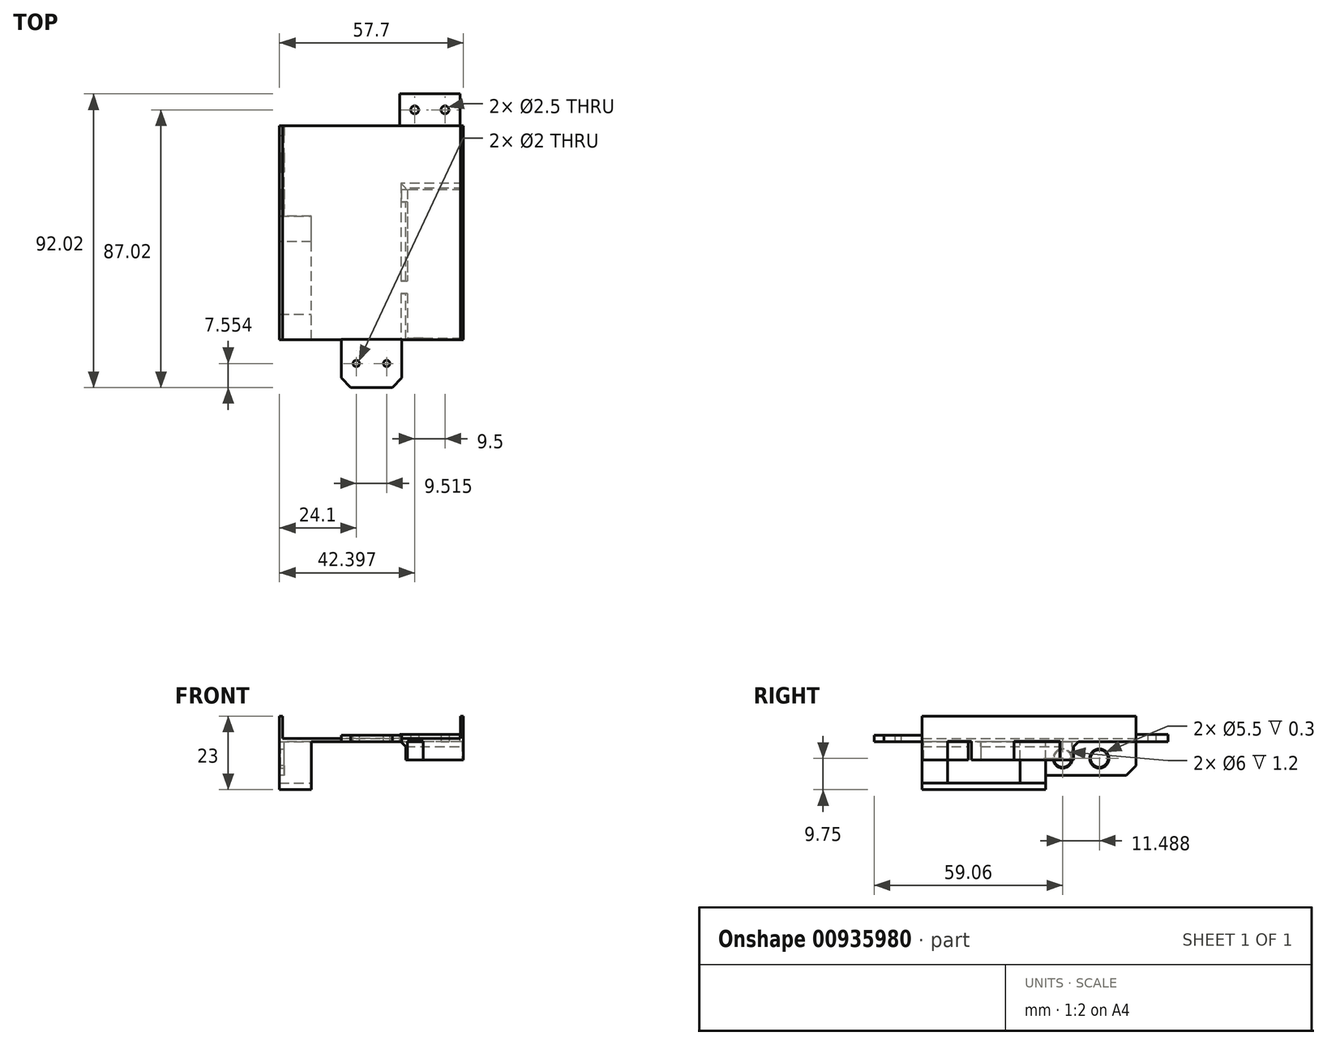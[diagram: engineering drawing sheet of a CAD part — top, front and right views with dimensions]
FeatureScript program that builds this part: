
annotation { "Feature Type Name" : "Feature", "Feature Type Description" : "" }
export const myFeature = defineFeature(function(context is Context, id is Id, definition is map)
    precondition{}
    {
        {
            var Q0;
            Q0=qCreatedBy(makeId("Top.planeOp"),FACE);
            var sketch = newSketch(context, id + "F0", { "sketchPlane" : qUnion([Q0])});
            skLineSegment(sketch, "E0.bottom", {"start": v(28.35, -33.5) * mm, "end": v(-28.35, -33.5) * mm});
            skLineSegment(sketch, "E0.top", {"start": v(28.35, 33.5) * mm, "end": v(-28.35, 33.5) * mm});
            skLineSegment(sketch, "E0.left", {"start": v(28.35, -33.5) * mm, "end": v(28.35, 33.5) * mm});
            skLineSegment(sketch, "E0.right", {"start": v(-28.35, -33.5) * mm, "end": v(-28.35, 33.5) * mm});
            skPoint(sketch, "E0.middle", {"position": v(0, 0) * mm});
            skLineSegment(sketch, "E1.bottom", {"start": v(27.85, -33.5) * mm, "end": v(-27.85, -33.5) * mm});
            skLineSegment(sketch, "E1.top", {"start": v(27.85, 33.5) * mm, "end": v(-27.85, 33.5) * mm});
            skLineSegment(sketch, "E1.left", {"start": v(27.85, -33.5) * mm, "end": v(27.85, 33.5) * mm});
            skLineSegment(sketch, "E1.right", {"start": v(-27.85, -33.5) * mm, "end": v(-27.85, 33.5) * mm});
            skSolve(sketch);
        }
        {
            var Q0;
            {var subQ0=sQuery(id+"F0.wireOp",EDGE,"E1.left");Q0=makeQuery(id+"F0.imprint","IMPRINT",FACE,{"disambiguationData":[TD([[makeQuery(id+"F0.imprint","IMPRINT",EDGE,{"derivedFrom":subQ0}),1.0]])]});}
            extrude(context, id + "F1", {"entities" : qUnion([Q0]), "depth" : 1 * mm, "offsetDistance" : 25 * mm});
        }
        {
            var Q0;
            Q0=makeQuery(id+"F1.opExtrude","CAP_FACE",FACE,{"disambiguationData":[OSD([sQuery(id+"F0.wireOp",EDGE,"E0.bottom"),sQuery(id+"F0.wireOp",EDGE,"E0.top"),sQuery(id+"F0.wireOp",EDGE,"E1.left"),sQuery(id+"F0.wireOp",EDGE,"E1.right")])],"isStart":false});
            var sketch = newSketch(context, id + "F2", { "sketchPlane" : qUnion([Q0])});
            skLineSegment(sketch, "E2.left", {"start": v(28.35, -33.5) * mm, "end": v(28.35, 33.5) * mm});
            skLineSegment(sketch, "E2.right", {"start": v(-28.35, -33.5) * mm, "end": v(-28.35, 33.5) * mm});
            skPoint(sketch, "E2.middle", {"position": v(0, 0) * mm});
            skLineSegment(sketch, "E3", {"start": v(-27.85, 33.5) * mm, "end": v(-28.35, 33.5) * mm});
            skLineSegment(sketch, "E4", {"start": v(27.85, 33.5) * mm, "end": v(28.35, 33.5) * mm});
            skLineSegment(sketch, "E5", {"start": v(-27.85, -33.5) * mm, "end": v(-28.35, -33.5) * mm});
            skLineSegment(sketch, "E6", {"start": v(27.85, -33.5) * mm, "end": v(28.35, -33.5) * mm});
            skPoint(sketch, "E7.orphan", {"position": v(28.35, -35) * mm});
            skPoint(sketch, "E8.orphan", {"position": v(-28.35, -35) * mm});
            skPoint(sketch, "E9.orphan", {"position": v(-28.35, 35) * mm});
            skPoint(sketch, "E10.orphan", {"position": v(28.35, 35) * mm});
            skSolve(sketch);
        }
        {
            var Q0;
            Q0=makeQuery(id+"F2.imprint","IMPRINT",FACE,{"disambiguationData":[TD([[makeQuery(id+"F2.imprint","IMPRINT",EDGE,{"derivedFrom":sQuery(id+"F2.wireOp",EDGE,"E2.right")}),-1.0]])]});
            extrude(context, id + "F3", {"entities" : qUnion([Q0]), "depth" : 7 * mm, "offsetDistance" : 25 * mm});
        }
        {
            var Q0;
            Q0=makeQuery(id+"F1.opExtrude","CAP_FACE",FACE,{"disambiguationData":[OSD([sQuery(id+"F0.wireOp",EDGE,"E0.bottom"),sQuery(id+"F0.wireOp",EDGE,"E0.top"),sQuery(id+"F0.wireOp",EDGE,"E1.left"),sQuery(id+"F0.wireOp",EDGE,"E1.right")])],"isStart":false});
            var sketch = newSketch(context, id + "F4", { "sketchPlane" : qUnion([Q0])});
            skLineSegment(sketch, "E11.bottom", {"start": v(27.85, 33.5) * mm, "end": v(28.85, 33.5) * mm});
            skLineSegment(sketch, "E11.top", {"start": v(27.85, -33.5) * mm, "end": v(28.85, -33.5) * mm});
            skLineSegment(sketch, "E11.left", {"start": v(27.85, 33.5) * mm, "end": v(27.85, -33.5) * mm});
            skLineSegment(sketch, "E11.right", {"start": v(28.85, 33.5) * mm, "end": v(28.85, -33.5) * mm});
            skSolve(sketch);
        }
        {
            var Q0;
            Q0 = qSketchRegion(id + "F4", true);
            extrude(context, id + "F5", {"entities" : qUnion([Q0]), "depth" : 7 * mm, "offsetDistance" : 25 * mm});
        }
        {
            var Q0;
            Q0=makeQuery(id+"F3.opExtrude","SWEPT_FACE",FACE,{"disambiguationData":[OSD([sQuery(id+"F2.wireOp",EDGE,"E2.right")])]});
            extrude(context, id + "F6", {"entities" : qUnion([Q0]), "operationType" : NewBodyOperationType.ADD, "depth" : .5 * mm, "offsetDistance" : 25 * mm});
        }
        {
            var Q0;
            {var subQ0=sQuery(id+"F2.wireOp",EDGE,"E2.right");Q0=makeQuery(id+"F6.boolean.opBoolean","MERGE",FACE,{"derivedFrom":[makeQuery(id+"F3.opExtrude","CAP_FACE",FACE,{"disambiguationData":[OSD([sQuery(id+"F0.wireOp",EDGE,"E1.right"),subQ0,sQuery(id+"F2.wireOp",EDGE,"E3"),sQuery(id+"F2.wireOp",EDGE,"E5")])],"isStart":true}),makeQuery(id+"F6.opExtrude","SWEPT_FACE",FACE,{"disambiguationData":[OSD([subQ0]),TDD([makeQuery(id+"F3.opExtrude","CAP_EDGE",EDGE,{"disambiguationData":[OSD([subQ0])],"isStart":true})])]})]});}
            extrude(context, id + "F7", {"entities" : qUnion([Q0]), "depth" : 1 * mm, "offsetDistance" : 25 * mm});
        }
        {
            var Q0;
            Q0=makeQuery(id+"F7.opExtrude","SWEPT_BODY",BODY,{"disambiguationData":[OSD([sQuery(id+"F0.wireOp",EDGE,"E1.right"),sQuery(id+"F2.wireOp",EDGE,"E2.right"),sQuery(id+"F2.wireOp",EDGE,"E3"),sQuery(id+"F2.wireOp",EDGE,"E5")])]});
            var Q1;
            Q1=makeQuery(id+"F1.opExtrude","SWEPT_BODY",BODY,{"disambiguationData":[OSD([sQuery(id+"F0.wireOp",EDGE,"E0.bottom"),sQuery(id+"F0.wireOp",EDGE,"E0.top"),sQuery(id+"F0.wireOp",EDGE,"E1.left"),sQuery(id+"F0.wireOp",EDGE,"E1.right")])]});
            var Q2;
            Q2=makeQuery(id+"F3.opExtrude","SWEPT_BODY",BODY,{"disambiguationData":[OSD([sQuery(id+"F0.wireOp",EDGE,"E1.right"),sQuery(id+"F2.wireOp",EDGE,"E2.right"),sQuery(id+"F2.wireOp",EDGE,"E3"),sQuery(id+"F2.wireOp",EDGE,"E5")])]});
            booleanBodies(context, id + "F8", {"operationType" : BooleanOperationType.UNION, "tools" : qUnion([Q0, Q1, Q2])});
        }
        {
            var Q0;
            Q0=makeQuery(id+"F5.opExtrude","CAP_FACE",FACE,{"disambiguationData":[OSD([sQuery(id+"F4.wireOp",EDGE,"E11.bottom"),sQuery(id+"F4.wireOp",EDGE,"E11.top"),sQuery(id+"F4.wireOp",EDGE,"E11.left"),sQuery(id+"F4.wireOp",EDGE,"E11.right")])],"isStart":true});
            extrude(context, id + "F9", {"entities" : qUnion([Q0]), "depth" : 1 * mm, "offsetDistance" : 25 * mm});
        }
        {
            var Q0;
            Q0=makeQuery(id+"F7.opExtrude","SWEPT_BODY",BODY,{"disambiguationData":[OSD([sQuery(id+"F0.wireOp",EDGE,"E1.right"),sQuery(id+"F2.wireOp",EDGE,"E2.right"),sQuery(id+"F2.wireOp",EDGE,"E3"),sQuery(id+"F2.wireOp",EDGE,"E5")])]});
            var Q1;
            Q1=makeQuery(id+"F9.opExtrude","SWEPT_BODY",BODY,{"disambiguationData":[OSD([sQuery(id+"F4.wireOp",EDGE,"E11.bottom"),sQuery(id+"F4.wireOp",EDGE,"E11.top"),sQuery(id+"F4.wireOp",EDGE,"E11.left"),sQuery(id+"F4.wireOp",EDGE,"E11.right")])]});
            var Q2;
            Q2=makeQuery(id+"F5.opExtrude","SWEPT_BODY",BODY,{"disambiguationData":[OSD([sQuery(id+"F4.wireOp",EDGE,"E11.bottom"),sQuery(id+"F4.wireOp",EDGE,"E11.top"),sQuery(id+"F4.wireOp",EDGE,"E11.left"),sQuery(id+"F4.wireOp",EDGE,"E11.right")])]});
            booleanBodies(context, id + "F10", {"operationType" : BooleanOperationType.UNION, "tools" : qUnion([Q0, Q1, Q2])});
        }
        {
            var Q0;
            {var subQ0=sQuery(id+"F0.wireOp",EDGE,"E1.right");Q0=makeQuery(id+"F10.opBoolean","MERGE",FACE,{"derivedFrom":[makeQuery(id+"F8.opBoolean","MERGE",FACE,{"derivedFrom":[makeQuery(id+"F1.opExtrude","CAP_FACE",FACE,{"disambiguationData":[OSD([sQuery(id+"F0.wireOp",EDGE,"E0.bottom"),sQuery(id+"F0.wireOp",EDGE,"E0.top"),sQuery(id+"F0.wireOp",EDGE,"E1.left"),subQ0])],"isStart":true}),makeQuery(id+"F7.opExtrude","CAP_FACE",FACE,{"disambiguationData":[OSD([subQ0,sQuery(id+"F2.wireOp",EDGE,"E2.right"),sQuery(id+"F2.wireOp",EDGE,"E3"),sQuery(id+"F2.wireOp",EDGE,"E5")])],"isStart":false})]}),makeQuery(id+"F9.opExtrude","CAP_FACE",FACE,{"disambiguationData":[OSD([sQuery(id+"F4.wireOp",EDGE,"E11.bottom"),sQuery(id+"F4.wireOp",EDGE,"E11.top"),sQuery(id+"F4.wireOp",EDGE,"E11.left"),sQuery(id+"F4.wireOp",EDGE,"E11.right")])],"isStart":false})]});}
            var sketch = newSketch(context, id + "F11", { "sketchPlane" : qUnion([Q0])});
            skLineSegment(sketch, "E12.bottom", {"start": v(-28.85, 33.5) * mm, "end": v(-18.85, 33.5) * mm});
            skLineSegment(sketch, "E12.top", {"start": v(-28.85, 25.5) * mm, "end": v(-18.85, 25.5) * mm});
            skLineSegment(sketch, "E12.left", {"start": v(-28.85, 33.5) * mm, "end": v(-28.85, 25.5) * mm});
            skLineSegment(sketch, "E12.right", {"start": v(-18.85, 33.5) * mm, "end": v(-18.85, 25.5) * mm});
            skSolve(sketch);
        }
        {
            var Q0;
            Q0 = qSketchRegion(id + "F11", true);
            extrude(context, id + "F12", {"entities" : qUnion([Q0]), "operationType" : NewBodyOperationType.ADD, "depth" : 13 * mm, "offsetDistance" : 25 * mm});
        }
        {
            var Q0;
            {var subQ0=sQuery(id+"F0.wireOp",EDGE,"E1.right");Q0=makeQuery(id+"F10.opBoolean","MERGE",FACE,{"derivedFrom":[makeQuery(id+"F8.opBoolean","MERGE",FACE,{"derivedFrom":[makeQuery(id+"F1.opExtrude","CAP_FACE",FACE,{"disambiguationData":[OSD([sQuery(id+"F0.wireOp",EDGE,"E0.bottom"),sQuery(id+"F0.wireOp",EDGE,"E0.top"),sQuery(id+"F0.wireOp",EDGE,"E1.left"),subQ0])],"isStart":true}),makeQuery(id+"F7.opExtrude","CAP_FACE",FACE,{"disambiguationData":[OSD([subQ0,sQuery(id+"F2.wireOp",EDGE,"E2.right"),sQuery(id+"F2.wireOp",EDGE,"E3"),sQuery(id+"F2.wireOp",EDGE,"E5")])],"isStart":false})]}),makeQuery(id+"F9.opExtrude","CAP_FACE",FACE,{"disambiguationData":[OSD([sQuery(id+"F4.wireOp",EDGE,"E11.bottom"),sQuery(id+"F4.wireOp",EDGE,"E11.top"),sQuery(id+"F4.wireOp",EDGE,"E11.left"),sQuery(id+"F4.wireOp",EDGE,"E11.right")])],"isStart":false})]});}
            var sketch = newSketch(context, id + "F13", { "sketchPlane" : qUnion([Q0])});
            skLineSegment(sketch, "E13", {"start": v(-18.85, 25.5) * mm, "end": v(-18.85, 2.82) * mm});
            skLineSegment(sketch, "E14.bottom", {"start": v(-18.85, 2.82) * mm, "end": v(-28.85, 2.82) * mm});
            skLineSegment(sketch, "E14.top", {"start": v(-18.85, -5.18) * mm, "end": v(-28.85, -5.18) * mm});
            skLineSegment(sketch, "E14.left", {"start": v(-18.85, 2.82) * mm, "end": v(-18.85, -5.18) * mm});
            skLineSegment(sketch, "E14.right", {"start": v(-28.85, 2.82) * mm, "end": v(-28.85, -5.18) * mm});
            skSolve(sketch);
        }
        {
            var Q0;
            Q0=makeQuery(id+"F13.imprint","IMPRINT",FACE,{"disambiguationData":[TD([[makeQuery(id+"F13.imprint","IMPRINT",EDGE,{"derivedFrom":sQuery(id+"F13.wireOp",EDGE,"E14.bottom")}),1.0]])]});
            extrude(context, id + "F14", {"entities" : qUnion([Q0]), "operationType" : NewBodyOperationType.ADD, "depth" : 13 * mm, "offsetDistance" : 25 * mm});
        }
        {
            var Q0;
            Q0=makeQuery(id+"F12.opExtrude","CAP_FACE",FACE,{"disambiguationData":[OSD([sQuery(id+"F11.wireOp",EDGE,"E12.bottom"),sQuery(id+"F11.wireOp",EDGE,"E12.top"),sQuery(id+"F11.wireOp",EDGE,"E12.left"),sQuery(id+"F11.wireOp",EDGE,"E12.right")])],"isStart":false});
            var sketch = newSketch(context, id + "F15", { "sketchPlane" : qUnion([Q0])});
            skLineSegment(sketch, "E15.bottom", {"start": v(-28.85, 33.5) * mm, "end": v(-18.83, 33.5) * mm});
            skLineSegment(sketch, "E15.top", {"start": v(-28.85, -5.2) * mm, "end": v(-18.83, -5.2) * mm});
            skLineSegment(sketch, "E15.left", {"start": v(-28.85, 33.5) * mm, "end": v(-28.85, -5.2) * mm});
            skLineSegment(sketch, "E15.right", {"start": v(-18.83, 33.5) * mm, "end": v(-18.83, -5.2) * mm});
            skSolve(sketch);
        }
        {
            var Q0;
            Q0 = qSketchRegion(id + "F15", true);
            extrude(context, id + "F16", {"entities" : qUnion([Q0]), "operationType" : NewBodyOperationType.ADD, "depth" : 2 * mm, "offsetDistance" : 25 * mm});
        }
        {
            var Q0;
            {var subQ0=sQuery(id+"F0.wireOp",EDGE,"E1.right");Q0=makeQuery(id+"F10.opBoolean","MERGE",FACE,{"derivedFrom":[makeQuery(id+"F8.opBoolean","MERGE",FACE,{"derivedFrom":[makeQuery(id+"F1.opExtrude","CAP_FACE",FACE,{"disambiguationData":[OSD([sQuery(id+"F0.wireOp",EDGE,"E0.bottom"),sQuery(id+"F0.wireOp",EDGE,"E0.top"),sQuery(id+"F0.wireOp",EDGE,"E1.left"),subQ0])],"isStart":true}),makeQuery(id+"F7.opExtrude","CAP_FACE",FACE,{"disambiguationData":[OSD([subQ0,sQuery(id+"F2.wireOp",EDGE,"E2.right"),sQuery(id+"F2.wireOp",EDGE,"E3"),sQuery(id+"F2.wireOp",EDGE,"E5")])],"isStart":false})]}),makeQuery(id+"F9.opExtrude","CAP_FACE",FACE,{"disambiguationData":[OSD([sQuery(id+"F4.wireOp",EDGE,"E11.bottom"),sQuery(id+"F4.wireOp",EDGE,"E11.top"),sQuery(id+"F4.wireOp",EDGE,"E11.left"),sQuery(id+"F4.wireOp",EDGE,"E11.right")])],"isStart":false})]});}
            var sketch = newSketch(context, id + "F17", { "sketchPlane" : qUnion([Q0])});
            skLineSegment(sketch, "E16.bottom", {"start": v(28.85, 33.5) * mm, "end": v(10.7, 33.5) * mm});
            skLineSegment(sketch, "E16.top", {"start": v(28.85, -14) * mm, "end": v(10.7, -14) * mm});
            skLineSegment(sketch, "E16.left", {"start": v(28.85, 33.5) * mm, "end": v(28.85, -14) * mm});
            skLineSegment(sketch, "E16.right", {"start": v(10.7, 33.5) * mm, "end": v(10.7, -14) * mm});
            skLineSegment(sketch, "E17.bottom", {"start": v(28.35, -13.5) * mm, "end": v(11.2, -13.5) * mm});
            skLineSegment(sketch, "E17.top", {"start": v(28.35, 33) * mm, "end": v(11.2, 33) * mm});
            skLineSegment(sketch, "E17.left", {"start": v(28.35, -13.5) * mm, "end": v(28.35, 33) * mm});
            skLineSegment(sketch, "E17.right", {"start": v(11.2, -13.5) * mm, "end": v(11.2, 33) * mm});
            skPoint(sketch, "E17.middle", {"position": v(19.78, 9.75) * mm});
            skPoint(sketch, "E18.start.orphan", {"position": v(10.7, 9.75) * mm});
            skPoint(sketch, "E19.start.orphan", {"position": v(19.78, 33.5) * mm});
            skSolve(sketch);
        }
        {
            var Q0;
            Q0=makeQuery(id+"F17.imprint","IMPRINT",FACE,{"disambiguationData":[TD([[makeQuery(id+"F17.imprint","IMPRINT",EDGE,{"derivedFrom":sQuery(id+"F17.wireOp",EDGE,"E16.bottom")}),1.0]])]});
            extrude(context, id + "F18", {"entities" : qUnion([Q0]), "operationType" : NewBodyOperationType.ADD, "depth" : 5.7 * mm, "offsetDistance" : 25 * mm});
        }
        {
            var Q0;
            Q0=makeQuery(id+"F18.opExtrude","CAP_FACE",FACE,{"disambiguationData":[OSD([sQuery(id+"F17.wireOp",EDGE,"E16.bottom"),sQuery(id+"F17.wireOp",EDGE,"E16.top"),sQuery(id+"F17.wireOp",EDGE,"E16.left"),sQuery(id+"F17.wireOp",EDGE,"E16.right"),sQuery(id+"F17.wireOp",EDGE,"E17.bottom"),sQuery(id+"F17.wireOp",EDGE,"E17.top"),sQuery(id+"F17.wireOp",EDGE,"E17.left"),sQuery(id+"F17.wireOp",EDGE,"E17.right")])],"isStart":false});
            var sketch = newSketch(context, id + "F19", { "sketchPlane" : qUnion([Q0])});
            skLineSegment(sketch, "E20", {"start": v(28.85, -9.71) * mm, "end": v(15.13, -9.71) * mm});
            skLineSegment(sketch, "E21", {"start": v(15.12, -13.5) * mm, "end": v(15.12, -8.74) * mm});
            skLineSegment(sketch, "E22", {"start": v(15.12, -8.74) * mm, "end": v(15.12, 4.76) * mm});
            skLineSegment(sketch, "E23", {"start": v(15.12, 4.76) * mm, "end": v(28.85, 4.76) * mm});
            skLineSegment(sketch, "E24", {"start": v(27.6, 33) * mm, "end": v(27.6, 25.6) * mm});
            skPoint(sketch, "E25.start.orphan", {"position": v(28.85, 25.6) * mm});
            skLineSegment(sketch, "E26", {"start": v(28.85, 25.6) * mm, "end": v(22.85, 25.6) * mm});
            skLineSegment(sketch, "E27", {"start": v(22.85, 25.6) * mm, "end": v(22.85, 18.09) * mm});
            skLineSegment(sketch, "E28", {"start": v(22.85, 18.09) * mm, "end": v(28.85, 18.09) * mm});
            skSolve(sketch);
        }
        {
            var Q0;
            {var subQ0=sQuery(id+"F19.wireOp",EDGE,"E26");var subQ1=makeQuery(id+"F18.opExtrude","CAP_EDGE",EDGE,{"disambiguationData":[OSD([sQuery(id+"F17.wireOp",EDGE,"E16.left")])],"isStart":false});var subQ2=makeQuery(id+"F19.imprint","INTERSECT",VERTEX,{"derivedFrom":[subQ1,subQ0]});Q0=makeQuery(id+"F19.imprint","IMPRINT",FACE,{"disambiguationData":[TD([[makeQuery(id+"F19.imprint","IMPRINT",EDGE,{"disambiguationData":[TD([[subQ2,-1.0]])],"derivedFrom":subQ0}),1.0]])]});}
            extrude(context, id + "F20", {"entities" : qUnion([Q0]), "operationType" : NewBodyOperationType.REMOVE, "oppositeDirection" : true, "depth" : 5.8 * mm, "offsetDistance" : 25 * mm});
        }
        {
            var Q0;
            {var subQ0=sQuery(id+"F19.wireOp",EDGE,"E20");var subQ1=makeQuery(id+"F18.opExtrude","CAP_EDGE",EDGE,{"disambiguationData":[OSD([sQuery(id+"F17.wireOp",EDGE,"E16.left")])],"isStart":false});var subQ2=makeQuery(id+"F19.imprint","INTERSECT",VERTEX,{"derivedFrom":[subQ1,subQ0]});Q0=makeQuery(id+"F19.imprint","IMPRINT",FACE,{"disambiguationData":[TD([[makeQuery(id+"F19.imprint","IMPRINT",EDGE,{"disambiguationData":[TD([[subQ2,-1.0]])],"derivedFrom":subQ0}),-1.0]])]});}
            extrude(context, id + "F21", {"entities" : qUnion([Q0]), "operationType" : NewBodyOperationType.REMOVE, "oppositeDirection" : true, "depth" : 5.8 * mm, "offsetDistance" : 25 * mm});
        }
        {
            var Q0;
            {var subQ5=makeQuery(id+"F18.opExtrude","CAP_EDGE",EDGE,{"disambiguationData":[OSD([sQuery(id+"F17.wireOp",EDGE,"E16.bottom")])],"isStart":false});Q0=makeQuery(id+"F19.imprint","IMPRINT",FACE,{"disambiguationData":[TD([[makeQuery(id+"F19.imprint","IMPRINT",EDGE,{"derivedFrom":subQ5}),1.0]])]});}
            var sketch = newSketch(context, id + "F22", { "sketchPlane" : qUnion([Q0])});
            skLineSegment(sketch, "E29", {"start": v(11.2, 33) * mm, "end": v(11.2, 33.5) * mm});
            skLineSegment(sketch, "E30", {"start": v(11.2, 33) * mm, "end": v(16.2, 33) * mm});
            skLineSegment(sketch, "E31", {"start": v(16.2, 33) * mm, "end": v(16.2, 33.5) * mm});
            skSolve(sketch);
        }
        {
            var Q0;
            {var subQ0=sQuery(id+"F22.wireOp",EDGE,"E30");Q0=makeQuery(id+"F22.imprint","IMPRINT",FACE,{"disambiguationData":[TD([[makeQuery(id+"F22.imprint","IMPRINT",EDGE,{"derivedFrom":subQ0}),1.0]])]});}
            extrude(context, id + "F23", {"entities" : qUnion([Q0]), "operationType" : NewBodyOperationType.REMOVE, "oppositeDirection" : true, "depth" : 5.8 * mm, "offsetDistance" : 25 * mm});
        }
        {
            var Q0;
            {var subQ5=makeQuery(id+"F18.opExtrude","CAP_EDGE",EDGE,{"disambiguationData":[OSD([sQuery(id+"F17.wireOp",EDGE,"E16.bottom")])],"isStart":false});Q0=makeQuery(id+"F19.imprint","IMPRINT",FACE,{"disambiguationData":[TD([[makeQuery(id+"F19.imprint","IMPRINT",EDGE,{"derivedFrom":subQ5}),1.0]])]});}
            var sketch = newSketch(context, id + "F24", { "sketchPlane" : qUnion([Q0])});
            skLineSegment(sketch, "E32", {"start": v(11.2, -13.5) * mm, "end": v(10.64, -13.5) * mm});
            skLineSegment(sketch, "E33", {"start": v(15.13, -9.69) * mm, "end": v(10.16, -9.69) * mm});
            skSolve(sketch);
        }
        {
            var Q0;
            {var subQ5=makeQuery(id+"F19.imprint","IMPRINT",EDGE,{"derivedFrom":makeQuery(id+"F18.opExtrude","CAP_EDGE",EDGE,{"disambiguationData":[OSD([sQuery(id+"F17.wireOp",EDGE,"E16.right")])],"isStart":false})});var subQ7=sQuery(id+"F24.wireOp",EDGE,"E33");var subQ8=makeQuery(id+"F24.imprint","INTERSECT",VERTEX,{"derivedFrom":[subQ5,subQ7]});Q0=makeQuery(id+"F24.imprint","IMPRINT",FACE,{"disambiguationData":[TD([[makeQuery(id+"F24.imprint","IMPRINT",EDGE,{"disambiguationData":[TD([[subQ8,1.0]])],"derivedFrom":subQ7}),1.0]])]});}
            extrude(context, id + "F25", {"entities" : qUnion([Q0]), "operationType" : NewBodyOperationType.REMOVE, "oppositeDirection" : true, "depth" : 5.6 * mm, "offsetDistance" : 25 * mm});
        }
        {
            var Q0;
            {var subQ5=makeQuery(id+"F18.opExtrude","CAP_EDGE",EDGE,{"disambiguationData":[OSD([sQuery(id+"F17.wireOp",EDGE,"E16.bottom")])],"isStart":false});Q0=makeQuery(id+"F19.imprint","IMPRINT",FACE,{"disambiguationData":[TD([[makeQuery(id+"F19.imprint","IMPRINT",EDGE,{"derivedFrom":subQ5}),1.0]])]});}
            var sketch = newSketch(context, id + "F26", { "sketchPlane" : qUnion([Q0])});
            skLineSegment(sketch, "E34", {"start": v(29.04, 19.08) * mm, "end": v(4.08, 19.08) * mm});
            skLineSegment(sketch, "E35", {"start": v(6.7, 19.08) * mm, "end": v(6.7, 15.08) * mm});
            skLineSegment(sketch, "E36", {"start": v(6.7, 15.08) * mm, "end": v(11.99, 15.08) * mm});
            skSolve(sketch);
        }
        {
            var Q0;
            {var subQ0=sQuery(id+"F26.wireOp",EDGE,"E34");var subQ1=makeQuery(id+"F19.imprint","IMPRINT",EDGE,{"derivedFrom":makeQuery(id+"F18.opExtrude","CAP_EDGE",EDGE,{"disambiguationData":[OSD([sQuery(id+"F17.wireOp",EDGE,"E17.right")])],"isStart":false})});var subQ2=makeQuery(id+"F26.imprint","INTERSECT",VERTEX,{"derivedFrom":[subQ1,subQ0]});Q0=makeQuery(id+"F26.imprint","IMPRINT",FACE,{"disambiguationData":[TD([[makeQuery(id+"F26.imprint","IMPRINT",EDGE,{"disambiguationData":[TD([[subQ2,-1.0]])],"derivedFrom":subQ0}),1.0]])]});}
            extrude(context, id + "F27", {"entities" : qUnion([Q0]), "operationType" : NewBodyOperationType.REMOVE, "oppositeDirection" : true, "depth" : 5.7 * mm, "offsetDistance" : 25 * mm});
        }
        {
            var Q0;
            {var subQ0=sQuery(id+"F17.wireOp",EDGE,"E17.right");var subQ1=sQuery(id+"F17.wireOp",EDGE,"E16.right");var subQ2=sQuery(id+"F4.wireOp",EDGE,"E11.right");var subQ3=sQuery(id+"F4.wireOp",EDGE,"E11.top");var subQ4=sQuery(id+"F4.wireOp",EDGE,"E11.bottom");var subQ5=sQuery(id+"F2.wireOp",EDGE,"E5");var subQ6=sQuery(id+"F2.wireOp",EDGE,"E3");var subQ7=sQuery(id+"F2.wireOp",EDGE,"E2.right");var subQ8=sQuery(id+"F0.wireOp",EDGE,"E1.right");var subQ9=sQuery(id+"F0.wireOp",EDGE,"E0.top");var subQ10=sQuery(id+"F0.wireOp",EDGE,"E0.bottom");var subQ11=makeQuery(id+"F10.opBoolean","MERGE",FACE,{"derivedFrom":[makeQuery(id+"F8.opBoolean","MERGE",FACE,{"derivedFrom":[makeQuery(id+"F1.opExtrude","CAP_FACE",FACE,{"disambiguationData":[OSD([subQ10,subQ9,sQuery(id+"F0.wireOp",EDGE,"E1.left"),subQ8])],"isStart":true}),makeQuery(id+"F7.opExtrude","CAP_FACE",FACE,{"disambiguationData":[OSD([subQ8,subQ7,subQ6,subQ5])],"isStart":false})]}),makeQuery(id+"F9.opExtrude","CAP_FACE",FACE,{"disambiguationData":[OSD([subQ4,subQ3,sQuery(id+"F4.wireOp",EDGE,"E11.left"),subQ2])],"isStart":false})]});Q0=makeQuery(id+"F27.boolean.opBoolean","MERGE",FACE,{"derivedFrom":[makeQuery(id+"F18.boolean.opBoolean","SPLIT",FACE,{"disambiguationData":[TD([makeQuery(id+"F1.opExtrude","SWEPT_FACE",FACE,{"disambiguationData":[OSD([subQ10])]})])],"derivedFrom":subQ11}),makeQuery(id+"F18.boolean.opBoolean","SPLIT",FACE,{"disambiguationData":[TD([makeQuery(id+"F18.opExtrude","SWEPT_FACE",FACE,{"disambiguationData":[OSD([sQuery(id+"F17.wireOp",EDGE,"E17.bottom")])]})])],"derivedFrom":subQ11})],"fromTools":[makeQuery(id+"F27.opExtrude","CAP_FACE",FACE,{"disambiguationData":[OSD([subQ1,subQ0,sQuery(id+"F26.wireOp",EDGE,"E34"),sQuery(id+"F26.wireOp",EDGE,"E36")])],"isStart":false})]});}
            var sketch = newSketch(context, id + "F28", { "sketchPlane" : qUnion([Q0])});
            skLineSegment(sketch, "E37.bottom", {"start": v(-28.85, -5.18) * mm, "end": v(-27.35, -5.18) * mm});
            skLineSegment(sketch, "E37.top", {"start": v(-28.85, -33.5) * mm, "end": v(-27.35, -33.5) * mm});
            skLineSegment(sketch, "E37.left", {"start": v(-28.85, -5.18) * mm, "end": v(-28.85, -33.5) * mm});
            skLineSegment(sketch, "E37.right", {"start": v(-27.35, -5.18) * mm, "end": v(-27.35, -33.5) * mm});
            skSolve(sketch);
        }
        {
            var Q0;
            Q0 = qSketchRegion(id + "F28", true);
            extrude(context, id + "F29", {"entities" : qUnion([Q0]), "operationType" : NewBodyOperationType.ADD, "depth" : 10.5 * mm, "offsetDistance" : 25 * mm});
        }
        {
            var Q0;
            Q0=makeQuery(id+"F29.opExtrude","CAP_EDGE",EDGE,{"disambiguationData":[OSD([sQuery(id+"F28.wireOp",EDGE,"E37.top")])],"isStart":false});
            chamfer(context, id + "F30", {"entities" : qUnion([Q0]), "width" : 3 * mm, "tangentPropagation" : true});
        }
        {
            var Q0;
            Q0=makeQuery(id+"F29.opExtrude","SWEPT_FACE",FACE,{"disambiguationData":[OSD([sQuery(id+"F28.wireOp",EDGE,"E37.right")])]});
            var sketch = newSketch(context, id + "F31", { "sketchPlane" : qUnion([Q0])});
            skLineSegment(sketch, "E38", {"start": v(27.45, -10.5) * mm, "end": v(27.45, 0) * mm});
            skLineSegment(sketch, "E39", {"start": v(27.45, -5.25) * mm, "end": v(24.78, -5.25) * mm});
            skLineSegment(sketch, "E40", {"start": v(16.32, 0) * mm, "end": v(16.32, -11.03) * mm});
            skPoint(sketch, "E40.startSnap0", {"position": v(16.32, -5.25) * mm});
            skCircle(sketch, "E41", {"center": v(22.03, -5.25) * mm, "radius": 2.75 * mm});
            skCircle(sketch, "E42", {"center": v(10.54, -5.25) * mm, "radius": 2.75 * mm});
            skLineSegment(sketch, "E43.trimOffspring", {"start": v(19.28, -5.25) * mm, "end": v(13.3, -5.25) * mm});
            skLineSegment(sketch, "E44.trimOffspring", {"start": v(7.8, -5.25) * mm, "end": v(5.18, -5.25) * mm});
            skSolve(sketch);
        }
        {
            var Q0;
            {var subQ0=sQuery(id+"F31.wireOp",EDGE,"E41");var subQ1=makeQuery(id+"F31.imprint","INTERSECT",VERTEX,{"derivedFrom":[sQuery(id+"F31.wireOp",EDGE,"E39"),subQ0]});Q0=makeQuery(id+"F31.imprint","IMPRINT",FACE,{"disambiguationData":[TD([[makeQuery(id+"F31.imprint","IMPRINT",EDGE,{"disambiguationData":[TD([[subQ1,-1.0]])],"derivedFrom":subQ0}),1.0]])]});}
            var Q1;
            {var subQ0=sQuery(id+"F31.wireOp",EDGE,"E42");var subQ1=makeQuery(id+"F31.imprint","INTERSECT",VERTEX,{"derivedFrom":[subQ0,sQuery(id+"F31.wireOp",EDGE,"E43.trimOffspring")]});Q1=makeQuery(id+"F31.imprint","IMPRINT",FACE,{"disambiguationData":[TD([[makeQuery(id+"F31.imprint","IMPRINT",EDGE,{"disambiguationData":[TD([[subQ1,-1.0]])],"derivedFrom":subQ0}),1.0]])]});}
            extrude(context, id + "F32", {"entities" : qUnion([Q0, Q1]), "operationType" : NewBodyOperationType.REMOVE, "oppositeDirection" : true, "depth" : 3 * mm, "offsetDistance" : 25 * mm});
        }
        {
            var Q0;
            Q0=makeQuery(id+"F29.opExtrude","SWEPT_FACE",FACE,{"disambiguationData":[OSD([sQuery(id+"F28.wireOp",EDGE,"E37.right")])]});
            var sketch = newSketch(context, id + "F33", { "sketchPlane" : qUnion([Q0])});
            skCircle(sketch, "E45", {"center": v(22.03, -5.25) * mm, "radius": 3 * mm});
            skCircle(sketch, "E46", {"center": v(10.54, -5.25) * mm, "radius": 3 * mm});
            skSolve(sketch);
        }
        {
            var Q0;
            Q0=makeQuery(id+"F33.imprint","IMPRINT",FACE,{"disambiguationData":[TD([[makeQuery(id+"F33.imprint","IMPRINT",EDGE,{"derivedFrom":sQuery(id+"F33.wireOp",EDGE,"E45")}),1.0]])]});
            var Q1;
            Q1=makeQuery(id+"F33.imprint","IMPRINT",FACE,{"disambiguationData":[TD([[makeQuery(id+"F33.imprint","IMPRINT",EDGE,{"derivedFrom":sQuery(id+"F33.wireOp",EDGE,"E46")}),1.0]])]});
            extrude(context, id + "F34", {"entities" : qUnion([Q0, Q1]), "operationType" : NewBodyOperationType.REMOVE, "oppositeDirection" : true, "depth" : 1.2 * mm, "offsetDistance" : 25 * mm});
        }
        {
            var Q0;
            Q0=makeQuery(id+"F18.opExtrude","CAP_EDGE",EDGE,{"disambiguationData":[OSD([sQuery(id+"F17.wireOp",EDGE,"E16.top")])],"isStart":true});
            chamfer(context, id + "F35", {"entities" : qUnion([Q0]), "chamferType" : ChamferType.OFFSET_ANGLE, "width" : 1.5 * mm, "oppositeDirection" : false, "angle" : 45 * degree, "tangentPropagation" : true});
        }
        {
            var Q0;
            {var subQ1=sQuery(id+"F17.wireOp",EDGE,"E16.right");Q0=makeQuery(id+"F27.boolean.opBoolean","SPLIT",EDGE,{"disambiguationData":[TD([makeQuery(id+"F18.opExtrude","SWEPT_FACE",FACE,{"disambiguationData":[OSD([sQuery(id+"F17.wireOp",EDGE,"E16.top")])]})])],"derivedFrom":makeQuery(id+"F18.opExtrude","CAP_EDGE",EDGE,{"disambiguationData":[OSD([subQ1])],"isStart":true})});}
            chamfer(context, id + "F36", {"entities" : qUnion([Q0]), "width" : 1.5 * mm, "tangentPropagation" : true});
        }
        {
            var Q0;
            {var subQ3=sQuery(id+"F0.wireOp",EDGE,"E0.bottom");var subQ5=sQuery(id+"F17.wireOp",EDGE,"E16.right");Q0=makeQuery(id+"F27.boolean.opBoolean","SPLIT",EDGE,{"disambiguationData":[TD([makeQuery(id+"F1.opExtrude","SWEPT_FACE",FACE,{"disambiguationData":[OSD([subQ3])]})])],"derivedFrom":makeQuery(id+"F18.opExtrude","CAP_EDGE",EDGE,{"disambiguationData":[OSD([subQ5])],"isStart":true})});}
            chamfer(context, id + "F37", {"entities" : qUnion([Q0]), "width" : 1.5 * mm, "tangentPropagation" : true});
        }
        {
            var Q0;
            {var subQ0=sQuery(id+"F4.wireOp",EDGE,"E11.bottom");var subQ1=sQuery(id+"F2.wireOp",EDGE,"E3");var subQ2=sQuery(id+"F2.wireOp",EDGE,"E2.right");Q0=makeQuery(id+"F29.boolean.opBoolean","MERGE",FACE,{"derivedFrom":[makeQuery(id+"F10.opBoolean","MERGE",FACE,{"derivedFrom":[makeQuery(id+"F5.opExtrude","SWEPT_FACE",FACE,{"disambiguationData":[OSD([subQ0])]}),makeQuery(id+"F8.opBoolean","MERGE",FACE,{"derivedFrom":[makeQuery(id+"F1.opExtrude","SWEPT_FACE",FACE,{"disambiguationData":[OSD([sQuery(id+"F0.wireOp",EDGE,"E0.top")])]}),makeQuery(id+"F6.boolean.opBoolean","MERGE",FACE,{"derivedFrom":[makeQuery(id+"F3.opExtrude","SWEPT_FACE",FACE,{"disambiguationData":[OSD([subQ1])]}),makeQuery(id+"F6.opExtrude","SWEPT_FACE",FACE,{"disambiguationData":[OSD([subQ2,subQ1])]})]}),makeQuery(id+"F7.opExtrude","SWEPT_FACE",FACE,{"disambiguationData":[OSD([subQ2,subQ1])]})]}),makeQuery(id+"F9.opExtrude","SWEPT_FACE",FACE,{"disambiguationData":[OSD([subQ0])]})]}),makeQuery(id+"F29.opExtrude","SWEPT_FACE",FACE,{"disambiguationData":[OSD([sQuery(id+"F28.wireOp",EDGE,"E37.top")])]})]});}
            var sketch = newSketch(context, id + "F38", { "sketchPlane" : qUnion([Q0])});
            skLineSegment(sketch, "E47.bottom", {"start": v(-27.8, 0) * mm, "end": v(-8.8, 0) * mm});
            skLineSegment(sketch, "E47.top", {"start": v(-27.8, 1) * mm, "end": v(-8.8, 1) * mm});
            skLineSegment(sketch, "E47.left", {"start": v(-27.8, 0) * mm, "end": v(-27.8, 1) * mm});
            skLineSegment(sketch, "E47.right", {"start": v(-8.8, 0) * mm, "end": v(-8.8, 1) * mm});
            skSolve(sketch);
        }
        {
            var Q0;
            Q0 = qSketchRegion(id + "F38", true);
            extrude(context, id + "F39", {"entities" : qUnion([Q0]), "operationType" : NewBodyOperationType.ADD, "depth" : 10 * mm, "offsetDistance" : 25 * mm});
        }
        {
            var Q0;
            {var subQ0=sQuery(id+"F17.wireOp",EDGE,"E17.right");var subQ1=sQuery(id+"F17.wireOp",EDGE,"E16.right");var subQ2=sQuery(id+"F4.wireOp",EDGE,"E11.right");var subQ3=sQuery(id+"F4.wireOp",EDGE,"E11.top");var subQ4=sQuery(id+"F4.wireOp",EDGE,"E11.bottom");var subQ5=sQuery(id+"F2.wireOp",EDGE,"E5");var subQ6=sQuery(id+"F2.wireOp",EDGE,"E3");var subQ7=sQuery(id+"F2.wireOp",EDGE,"E2.right");var subQ8=sQuery(id+"F0.wireOp",EDGE,"E1.right");var subQ9=sQuery(id+"F0.wireOp",EDGE,"E0.top");var subQ10=sQuery(id+"F0.wireOp",EDGE,"E0.bottom");var subQ11=makeQuery(id+"F10.opBoolean","MERGE",FACE,{"derivedFrom":[makeQuery(id+"F8.opBoolean","MERGE",FACE,{"derivedFrom":[makeQuery(id+"F1.opExtrude","CAP_FACE",FACE,{"disambiguationData":[OSD([subQ10,subQ9,sQuery(id+"F0.wireOp",EDGE,"E1.left"),subQ8])],"isStart":true}),makeQuery(id+"F7.opExtrude","CAP_FACE",FACE,{"disambiguationData":[OSD([subQ8,subQ7,subQ6,subQ5])],"isStart":false})]}),makeQuery(id+"F9.opExtrude","CAP_FACE",FACE,{"disambiguationData":[OSD([subQ4,subQ3,sQuery(id+"F4.wireOp",EDGE,"E11.left"),subQ2])],"isStart":false})]});Q0=makeQuery(id+"F39.boolean.opBoolean","MERGE",FACE,{"derivedFrom":[makeQuery(id+"F27.boolean.opBoolean","MERGE",FACE,{"derivedFrom":[makeQuery(id+"F18.boolean.opBoolean","SPLIT",FACE,{"disambiguationData":[TD([makeQuery(id+"F1.opExtrude","SWEPT_FACE",FACE,{"disambiguationData":[OSD([subQ10])]})])],"derivedFrom":subQ11}),makeQuery(id+"F18.boolean.opBoolean","SPLIT",FACE,{"disambiguationData":[TD([makeQuery(id+"F18.opExtrude","SWEPT_FACE",FACE,{"disambiguationData":[OSD([sQuery(id+"F17.wireOp",EDGE,"E17.bottom")])]})])],"derivedFrom":subQ11})],"fromTools":[makeQuery(id+"F27.opExtrude","CAP_FACE",FACE,{"disambiguationData":[OSD([subQ1,subQ0,sQuery(id+"F26.wireOp",EDGE,"E34"),sQuery(id+"F26.wireOp",EDGE,"E36")])],"isStart":false})]}),makeQuery(id+"F39.opExtrude","SWEPT_FACE",FACE,{"disambiguationData":[OSD([sQuery(id+"F38.wireOp",EDGE,"E47.bottom")])]})]});}
            var sketch = newSketch(context, id + "F40", { "sketchPlane" : qUnion([Q0])});
            skLineSegment(sketch, "E48", {"start": v(8.8, -38.5) * mm, "end": v(12.3, -38.5) * mm});
            skLineSegment(sketch, "E49", {"start": v(18.3, -38.5) * mm, "end": v(18.3, -44.62) * mm});
            skLineSegment(sketch, "E50", {"start": v(18.3, -38.5) * mm, "end": v(18.3, -37.4) * mm});
            skLineSegment(sketch, "E51", {"start": v(8.8, -39.27) * mm, "end": v(12.56, -39.27) * mm});
            skLineSegment(sketch, "E52", {"start": v(27.8, -39.55) * mm, "end": v(23.72, -39.55) * mm});
            skCircle(sketch, "E53", {"center": v(13.55, -38.5) * mm, "radius": 1.25 * mm});
            skCircle(sketch, "E54", {"center": v(23.05, -38.5) * mm, "radius": 1.25 * mm});
            skLineSegment(sketch, "E55.trimOffspring", {"start": v(14.8, -38.5) * mm, "end": v(21.8, -38.5) * mm});
            skLineSegment(sketch, "E56.trimOffspring", {"start": v(13.55, -37.25) * mm, "end": v(13.55, -36.66) * mm});
            skLineSegment(sketch, "E57.trimOffspring", {"start": v(24.3, -38.5) * mm, "end": v(27.8, -38.5) * mm});
            skSolve(sketch);
        }
        {
            var Q0;
            {var subQ0=sQuery(id+"F40.wireOp",EDGE,"E53");var subQ2=makeQuery(id+"F40.imprint","IMPRINT",VERTEX,{"derivedFrom":subQ0});Q0=makeQuery(id+"F40.imprint","IMPRINT",FACE,{"disambiguationData":[TD([[makeQuery(id+"F40.imprint","IMPRINT",EDGE,{"disambiguationData":[TD([[subQ2,1.0]])],"derivedFrom":subQ0}),1.0]])]});}
            var Q1;
            {var subQ0=sQuery(id+"F40.wireOp",EDGE,"E54");var subQ1=makeQuery(id+"F40.imprint","INTERSECT",VERTEX,{"derivedFrom":[subQ0,sQuery(id+"F40.wireOp",EDGE,"E55.trimOffspring")]});Q1=makeQuery(id+"F40.imprint","IMPRINT",FACE,{"disambiguationData":[TD([[makeQuery(id+"F40.imprint","IMPRINT",EDGE,{"disambiguationData":[TD([[subQ1,1.0]])],"derivedFrom":subQ0}),1.0]])]});}
            extrude(context, id + "F41", {"entities" : qUnion([Q0, Q1]), "operationType" : NewBodyOperationType.REMOVE, "oppositeDirection" : true, "depth" : 3 * mm, "offsetDistance" : 25 * mm});
        }
        {
            var Q0;
            {var subQ0=sQuery(id+"F17.wireOp",EDGE,"E17.right");var subQ1=sQuery(id+"F17.wireOp",EDGE,"E16.right");var subQ2=sQuery(id+"F4.wireOp",EDGE,"E11.right");var subQ3=sQuery(id+"F4.wireOp",EDGE,"E11.top");var subQ4=sQuery(id+"F4.wireOp",EDGE,"E11.bottom");var subQ5=sQuery(id+"F2.wireOp",EDGE,"E5");var subQ6=sQuery(id+"F2.wireOp",EDGE,"E3");var subQ7=sQuery(id+"F2.wireOp",EDGE,"E2.right");var subQ8=sQuery(id+"F0.wireOp",EDGE,"E1.right");var subQ9=sQuery(id+"F0.wireOp",EDGE,"E0.top");var subQ10=sQuery(id+"F0.wireOp",EDGE,"E0.bottom");var subQ11=makeQuery(id+"F10.opBoolean","MERGE",FACE,{"derivedFrom":[makeQuery(id+"F8.opBoolean","MERGE",FACE,{"derivedFrom":[makeQuery(id+"F1.opExtrude","CAP_FACE",FACE,{"disambiguationData":[OSD([subQ10,subQ9,sQuery(id+"F0.wireOp",EDGE,"E1.left"),subQ8])],"isStart":true}),makeQuery(id+"F7.opExtrude","CAP_FACE",FACE,{"disambiguationData":[OSD([subQ8,subQ7,subQ6,subQ5])],"isStart":false})]}),makeQuery(id+"F9.opExtrude","CAP_FACE",FACE,{"disambiguationData":[OSD([subQ4,subQ3,sQuery(id+"F4.wireOp",EDGE,"E11.left"),subQ2])],"isStart":false})]});Q0=makeQuery(id+"F39.boolean.opBoolean","MERGE",FACE,{"derivedFrom":[makeQuery(id+"F27.boolean.opBoolean","MERGE",FACE,{"derivedFrom":[makeQuery(id+"F18.boolean.opBoolean","SPLIT",FACE,{"disambiguationData":[TD([makeQuery(id+"F1.opExtrude","SWEPT_FACE",FACE,{"disambiguationData":[OSD([subQ10])]})])],"derivedFrom":subQ11}),makeQuery(id+"F18.boolean.opBoolean","SPLIT",FACE,{"disambiguationData":[TD([makeQuery(id+"F18.opExtrude","SWEPT_FACE",FACE,{"disambiguationData":[OSD([sQuery(id+"F17.wireOp",EDGE,"E17.bottom")])]})])],"derivedFrom":subQ11})],"fromTools":[makeQuery(id+"F27.opExtrude","CAP_FACE",FACE,{"disambiguationData":[OSD([subQ1,subQ0,sQuery(id+"F26.wireOp",EDGE,"E34"),sQuery(id+"F26.wireOp",EDGE,"E36")])],"isStart":false})]}),makeQuery(id+"F39.opExtrude","SWEPT_FACE",FACE,{"disambiguationData":[OSD([sQuery(id+"F38.wireOp",EDGE,"E47.bottom")])]})]});}
            var sketch = newSketch(context, id + "F42", { "sketchPlane" : qUnion([Q0])});
            skLineSegment(sketch, "E58", {"start": v(0, 33.52) * mm, "end": v(-9.5, 33.52) * mm});
            skLineSegment(sketch, "E59.bottom", {"start": v(-9.5, 33.52) * mm, "end": v(9.5, 33.52) * mm});
            skLineSegment(sketch, "E59.top", {"start": v(-9.5, 48.52) * mm, "end": v(9.5, 48.52) * mm});
            skLineSegment(sketch, "E59.left", {"start": v(-9.5, 33.52) * mm, "end": v(-9.5, 48.52) * mm});
            skLineSegment(sketch, "E59.right", {"start": v(9.5, 33.52) * mm, "end": v(9.5, 48.52) * mm});
            skSolve(sketch);
        }
        {
            var Q0;
            Q0 = qSketchRegion(id + "F42", true);
            extrude(context, id + "F43", {"entities" : qUnion([Q0]), "oppositeDirection" : true, "depth" : 2 * mm, "offsetDistance" : 25 * mm});
        }
        {
            var Q0;
            Q0=makeQuery(id+"F43.opExtrude","SWEPT_FACE",FACE,{"disambiguationData":[OSD([sQuery(id+"F42.wireOp",EDGE,"E59.bottom")])]});
            extrude(context, id + "F44", {"entities" : qUnion([Q0]), "depth" : .1 * mm, "offsetDistance" : 25 * mm});
        }
        {
            var Q0;
            Q0=makeQuery(id+"F7.opExtrude","SWEPT_BODY",BODY,{"disambiguationData":[OSD([sQuery(id+"F0.wireOp",EDGE,"E1.right"),sQuery(id+"F2.wireOp",EDGE,"E2.right"),sQuery(id+"F2.wireOp",EDGE,"E3"),sQuery(id+"F2.wireOp",EDGE,"E5")])]});
            var Q1;
            Q1=makeQuery(id+"F44.opExtrude","SWEPT_BODY",BODY,{"disambiguationData":[OSD([sQuery(id+"F42.wireOp",EDGE,"E59.bottom")])]});
            var Q2;
            Q2=makeQuery(id+"F43.opExtrude","SWEPT_BODY",BODY,{"disambiguationData":[OSD([sQuery(id+"F42.wireOp",EDGE,"E59.bottom"),sQuery(id+"F42.wireOp",EDGE,"E59.top"),sQuery(id+"F42.wireOp",EDGE,"E59.left"),sQuery(id+"F42.wireOp",EDGE,"E59.right")])]});
            booleanBodies(context, id + "F45", {"operationType" : BooleanOperationType.UNION, "tools" : qUnion([Q0, Q1, Q2])});
        }
        {
            var Q0;
            {var subQ0=sQuery(id+"F0.wireOp",EDGE,"E1.right");Q0=makeQuery(id+"F39.boolean.opBoolean","MERGE",FACE,{"derivedFrom":[makeQuery(id+"F8.opBoolean","MERGE",FACE,{"derivedFrom":[makeQuery(id+"F1.opExtrude","CAP_FACE",FACE,{"disambiguationData":[OSD([sQuery(id+"F0.wireOp",EDGE,"E0.bottom"),sQuery(id+"F0.wireOp",EDGE,"E0.top"),sQuery(id+"F0.wireOp",EDGE,"E1.left"),subQ0])],"isStart":false}),makeQuery(id+"F7.opExtrude","CAP_FACE",FACE,{"disambiguationData":[OSD([subQ0,sQuery(id+"F2.wireOp",EDGE,"E2.right"),sQuery(id+"F2.wireOp",EDGE,"E3"),sQuery(id+"F2.wireOp",EDGE,"E5")])],"isStart":true})]}),makeQuery(id+"F39.opExtrude","SWEPT_FACE",FACE,{"disambiguationData":[OSD([sQuery(id+"F38.wireOp",EDGE,"E47.top")])]})]});}
            var sketch = newSketch(context, id + "F46", { "sketchPlane" : qUnion([Q0])});
            skLineSegment(sketch, "E60", {"start": v(8.8, 33.5) * mm, "end": v(27.85, 33.5) * mm});
            skSolve(sketch);
        }
        {
            var Q0;
            {var subQ1=sQuery(id+"F38.wireOp",EDGE,"E47.top");Q0=makeQuery(id+"F46.imprint","IMPRINT",FACE,{"disambiguationData":[TD([[makeQuery(id+"F46.imprint","IMPRINT",EDGE,{"derivedFrom":makeQuery(id+"F39.opExtrude","CAP_EDGE",EDGE,{"disambiguationData":[OSD([subQ1])],"isStart":false})}),1.0]])]});}
            extrude(context, id + "F47", {"entities" : qUnion([Q0]), "operationType" : NewBodyOperationType.ADD, "depth" : 1.25 * mm, "offsetDistance" : 25 * mm});
        }
        {
            var Q0;
            {var subQ0=sQuery(id+"F42.wireOp",EDGE,"E59.bottom");Q0=makeQuery(id+"F45.opBoolean","MERGE",FACE,{"derivedFrom":[makeQuery(id+"F43.opExtrude","CAP_FACE",FACE,{"disambiguationData":[OSD([subQ0,sQuery(id+"F42.wireOp",EDGE,"E59.top"),sQuery(id+"F42.wireOp",EDGE,"E59.left"),sQuery(id+"F42.wireOp",EDGE,"E59.right")])],"isStart":false}),makeQuery(id+"F44.opExtrude","SWEPT_FACE",FACE,{"disambiguationData":[OSD([subQ0]),TDD([makeQuery(id+"F43.opExtrude","CAP_EDGE",EDGE,{"disambiguationData":[OSD([subQ0])],"isStart":false})])]})]});}
            var sketch = newSketch(context, id + "F48", { "sketchPlane" : qUnion([Q0])});
            skLineSegment(sketch, "E61", {"start": v(9.5, -40.97) * mm, "end": v(5.76, -40.97) * mm});
            skLineSegment(sketch, "E62", {"start": v(9.5, -38.98) * mm, "end": v(4.75, -38.98) * mm});
            skCircle(sketch, "E63", {"center": v(4.76, -40.97) * mm, "radius": 1 * mm});
            skLineSegment(sketch, "E64", {"start": v(-9.5, -39.54) * mm, "end": v(-4.75, -39.54) * mm});
            skLineSegment(sketch, "E65", {"start": v(-4.75, -39.54) * mm, "end": v(-4.75, -39.97) * mm});
            skCircle(sketch, "E66", {"center": v(-4.75, -40.97) * mm, "radius": 1 * mm});
            skLineSegment(sketch, "E67.trimOffspring", {"start": v(3.76, -40.97) * mm, "end": v(-3.75, -40.97) * mm});
            skLineSegment(sketch, "E68.trimOffspring", {"start": v(-5.75, -40.97) * mm, "end": v(-9.5, -40.97) * mm});
            skLineSegment(sketch, "E69.trimOffspring", {"start": v(-4.75, -41.97) * mm, "end": v(-4.75, -42.6) * mm});
            skSolve(sketch);
        }
        {
            var Q0;
            {var subQ0=sQuery(id+"F48.wireOp",EDGE,"E63");var subQ1=makeQuery(id+"F48.imprint","INTERSECT",VERTEX,{"derivedFrom":[sQuery(id+"F48.wireOp",EDGE,"E61"),subQ0]});Q0=makeQuery(id+"F48.imprint","IMPRINT",FACE,{"disambiguationData":[TD([[makeQuery(id+"F48.imprint","IMPRINT",EDGE,{"disambiguationData":[TD([[subQ1,-1.0]])],"derivedFrom":subQ0}),1.0]])]});}
            var Q1;
            {var subQ0=sQuery(id+"F48.wireOp",EDGE,"E66");var subQ4=makeQuery(id+"F48.imprint","IMPRINT",VERTEX,{"derivedFrom":subQ0});Q1=makeQuery(id+"F48.imprint","IMPRINT",FACE,{"disambiguationData":[TD([[makeQuery(id+"F48.imprint","IMPRINT",EDGE,{"disambiguationData":[TD([[subQ4,1.0]])],"derivedFrom":subQ0}),1.0]])]});}
            extrude(context, id + "F49", {"entities" : qUnion([Q0, Q1]), "operationType" : NewBodyOperationType.REMOVE, "oppositeDirection" : true, "depth" : 3 * mm, "offsetDistance" : 25 * mm});
        }
        {
            var Q0;
            Q0=makeQuery(id+"F43.opExtrude","SWEPT_EDGE",EDGE,{"disambiguationData":[OSD([sQuery(id+"F42.wireOp",EDGE,"E59.top"),sQuery(id+"F42.wireOp",EDGE,"E59.right")])]});
            chamfer(context, id + "F50", {"entities" : qUnion([Q0]), "width" : 3 * mm, "tangentPropagation" : true});
        }
        {
            var Q0;
            Q0=makeQuery(id+"F43.opExtrude","SWEPT_EDGE",EDGE,{"disambiguationData":[OSD([sQuery(id+"F42.wireOp",EDGE,"E59.top"),sQuery(id+"F42.wireOp",EDGE,"E59.left")])]});
            chamfer(context, id + "F51", {"entities" : qUnion([Q0]), "width" : 3 * mm, "tangentPropagation" : true});
        }
    });
